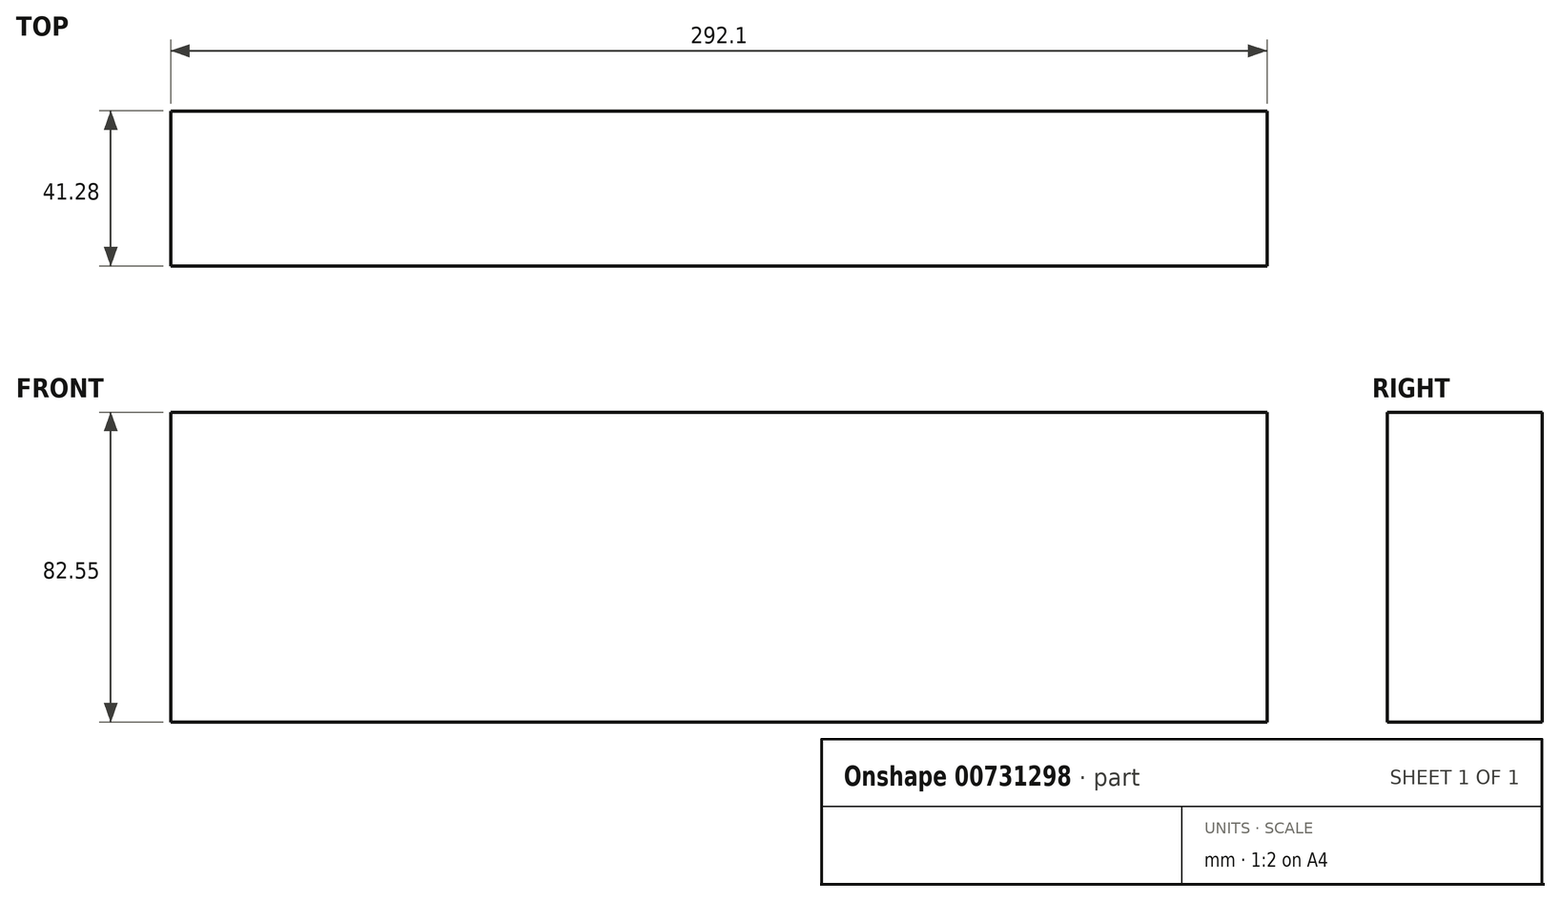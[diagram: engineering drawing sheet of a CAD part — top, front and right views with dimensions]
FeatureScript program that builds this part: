
annotation { "Feature Type Name" : "Feature", "Feature Type Description" : "" }
export const myFeature = defineFeature(function(context is Context, id is Id, definition is map)
    precondition{}
    {
        {
            var Q0;
            Q0=qCreatedBy(makeId("Top.planeOp"),FACE);
            var sketch = newSketch(context, id + "F0", { "sketchPlane" : qUnion([Q0])});
            skLineSegment(sketch, "E0", {"start": v(0, 0) * mm, "end": v(0, 19.4) * mm});
            skLineSegment(sketch, "E1", {"start": v(0, 19.4) * mm, "end": v(-292.1, 19.4) * mm});
            skLineSegment(sketch, "E2", {"start": v(-292.1, 19.4) * mm, "end": v(-292.1, -21.87) * mm});
            skLineSegment(sketch, "E3", {"start": v(-292.1, -21.87) * mm, "end": v(0, -21.87) * mm});
            skLineSegment(sketch, "E4", {"start": v(0, -21.87) * mm, "end": v(0, 0) * mm});
            skSolve(sketch);
        }
        {
            var Q0;
            Q0=makeQuery(id+"F0.imprint","IMPRINT",FACE,{"disambiguationData":[TD([[makeQuery(id+"F0.imprint","IMPRINT",EDGE,{"derivedFrom":sQuery(id+"F0.wireOp",EDGE,"E0")}),1.0]])]});
            extrude(context, id + "F1", {"entities" : qUnion([Q0]), "depth" : 82.55 * mm, "offsetDistance" : 25.4 * mm});
        }
    });
